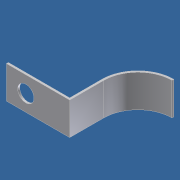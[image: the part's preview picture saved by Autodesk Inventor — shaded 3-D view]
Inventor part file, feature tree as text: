
AUTODESK INVENTOR PART (.ipt)
format: ipt  version: unknown  size: 186,880 bytes
history: native  units: mm
features: sketch x2, extrude x1, hole x1
ambient origin geometry x8: Origin, YZ Plane, XZ Plane, XY Plane, X Axis, Y Axis, Z Axis, Center Point
bodies: Solido1 (feature_tree)
feature tree (4):
  extrude  "Estrusione1"  Depth=10.0mm TaperAngle=0.0deg
  hole  "Foro2"  [1 undecoded]
  sketch  "Schizzo1"
  sketch  "Schizzo3"
note: 1 required parameter value undecoded (feature->parameter linkage not recoverable at this tier; creation-order binding heuristic only, values carry confidence <= 0.55)
